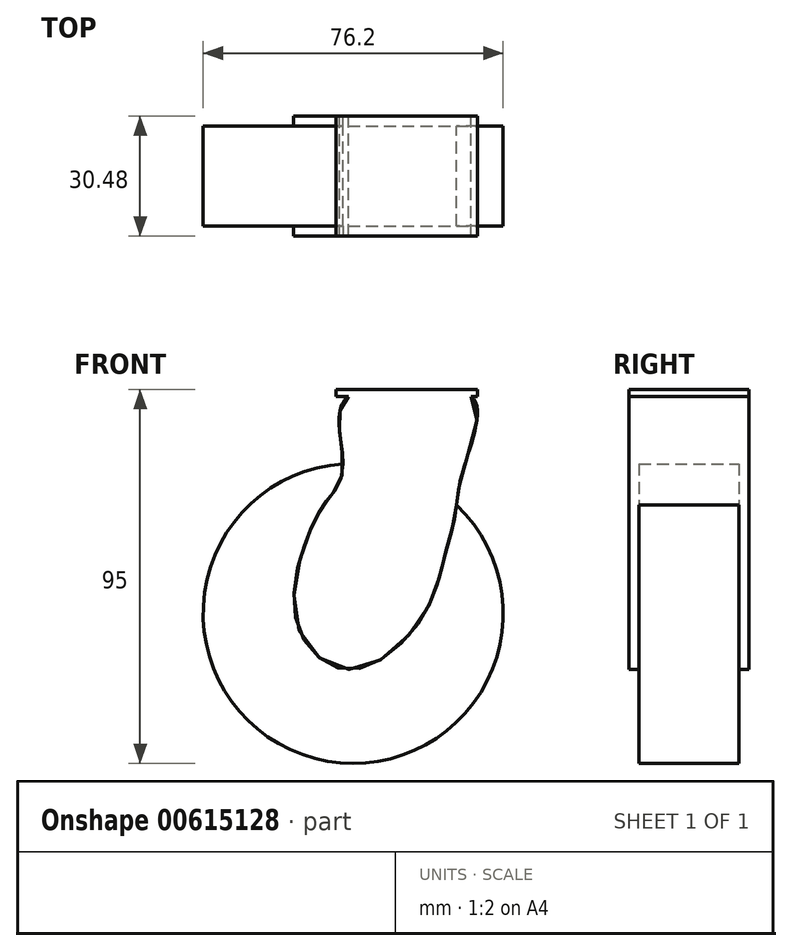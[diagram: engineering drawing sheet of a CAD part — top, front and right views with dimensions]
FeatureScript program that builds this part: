
annotation { "Feature Type Name" : "Feature", "Feature Type Description" : "" }
export const myFeature = defineFeature(function(context is Context, id is Id, definition is map)
    precondition{}
    {
        {
            var Q0;
            Q0=qCreatedBy(makeId("Front.planeOp"),FACE);
            var sketch = newSketch(context, id + "F0", { "sketchPlane" : qUnion([Q0])});
            skCircle(sketch, "E0", {"center": v(0, 0) * mm, "radius": 38.1 * mm});
            skSolve(sketch);
        }
        {
            var Q0;
            Q0=qCreatedBy(makeId("Front.planeOp"),FACE);
            var sketch = newSketch(context, id + "F1", { "sketchPlane" : qUnion([Q0])});
            skFitSpline(sketch, "E1", {"points": [v(-14.2, -2.94) * mm, v(0, -14.21) * mm, v(18.12, 0) * mm, v(23.17, 14.26) * mm, v(25.84, 24.65) * mm, v(27.62, 35.32) * mm, v(30.94, 54.08) * mm, v(15.25, 56.79) * mm, v(0, 55.89) * mm, v(-3.23, 51.94) * mm, v(-3.23, 44.52) * mm, v(-2.94, 34.73) * mm, v(-6.8, 28.5) * mm, v(-11.54, 19.6) * mm, v(-14.2, -2.94) * mm]});
            skSolve(sketch);
        }
        {
            var Q0;
            Q0=makeQuery(id+"F0.imprint","IMPRINT",FACE,{"disambiguationData":[TD([[makeQuery(id+"F0.imprint","IMPRINT",EDGE,{"derivedFrom":sQuery(id+"F0.wireOp",EDGE,"E0")}),1.0]])]});
            extrude(context, id + "F2", {"entities" : qUnion([Q0]), "depth" : 25.4 * mm});
        }
        {
            var Q0;
            Q0=makeQuery(id+"F1.imprint","IMPRINT",FACE,{"disambiguationData":[TD([[makeQuery(id+"F1.imprint","IMPRINT",EDGE,{"derivedFrom":sQuery(id+"F1.wireOp",EDGE,"E1")}),1.0]])]});
            extrude(context, id + "F3", {"entities" : qUnion([Q0]), "operationType" : NewBodyOperationType.ADD, "depth" : 27.94 * mm, "hasSecondDirection" : true, "secondDirectionOppositeDirection" : true, "secondDirectionDepth" : 2.54 * mm});
        }
        {
            var Q0;
            Q0=qCreatedBy(makeId("Front.planeOp"),FACE);
            var sketch = newSketch(context, id + "F4", { "sketchPlane" : qUnion([Q0])});
            skLineSegment(sketch, "E2.bottom", {"start": v(-4.39, 55.16) * mm, "end": v(31.6, 55.16) * mm});
            skLineSegment(sketch, "E2.top", {"start": v(-4.39, 56.9) * mm, "end": v(31.6, 56.9) * mm});
            skLineSegment(sketch, "E2.left", {"start": v(-4.39, 56.9) * mm, "end": v(-4.39, 55.16) * mm});
            skLineSegment(sketch, "E2.right", {"start": v(31.6, 56.9) * mm, "end": v(31.6, 55.16) * mm});
            skSolve(sketch);
        }
        {
            var Q0;
            Q0=makeQuery(id+"F4.imprint","IMPRINT",FACE,{"disambiguationData":[TD([[makeQuery(id+"F4.imprint","IMPRINT",EDGE,{"derivedFrom":sQuery(id+"F4.wireOp",EDGE,"E2.bottom")}),1.0]])]});
            extrude(context, id + "F5", {"entities" : qUnion([Q0]), "operationType" : NewBodyOperationType.ADD, "depth" : 27.94 * mm, "hasSecondDirection" : true, "secondDirectionOppositeDirection" : true, "secondDirectionDepth" : 2.54 * mm});
        }
    });
